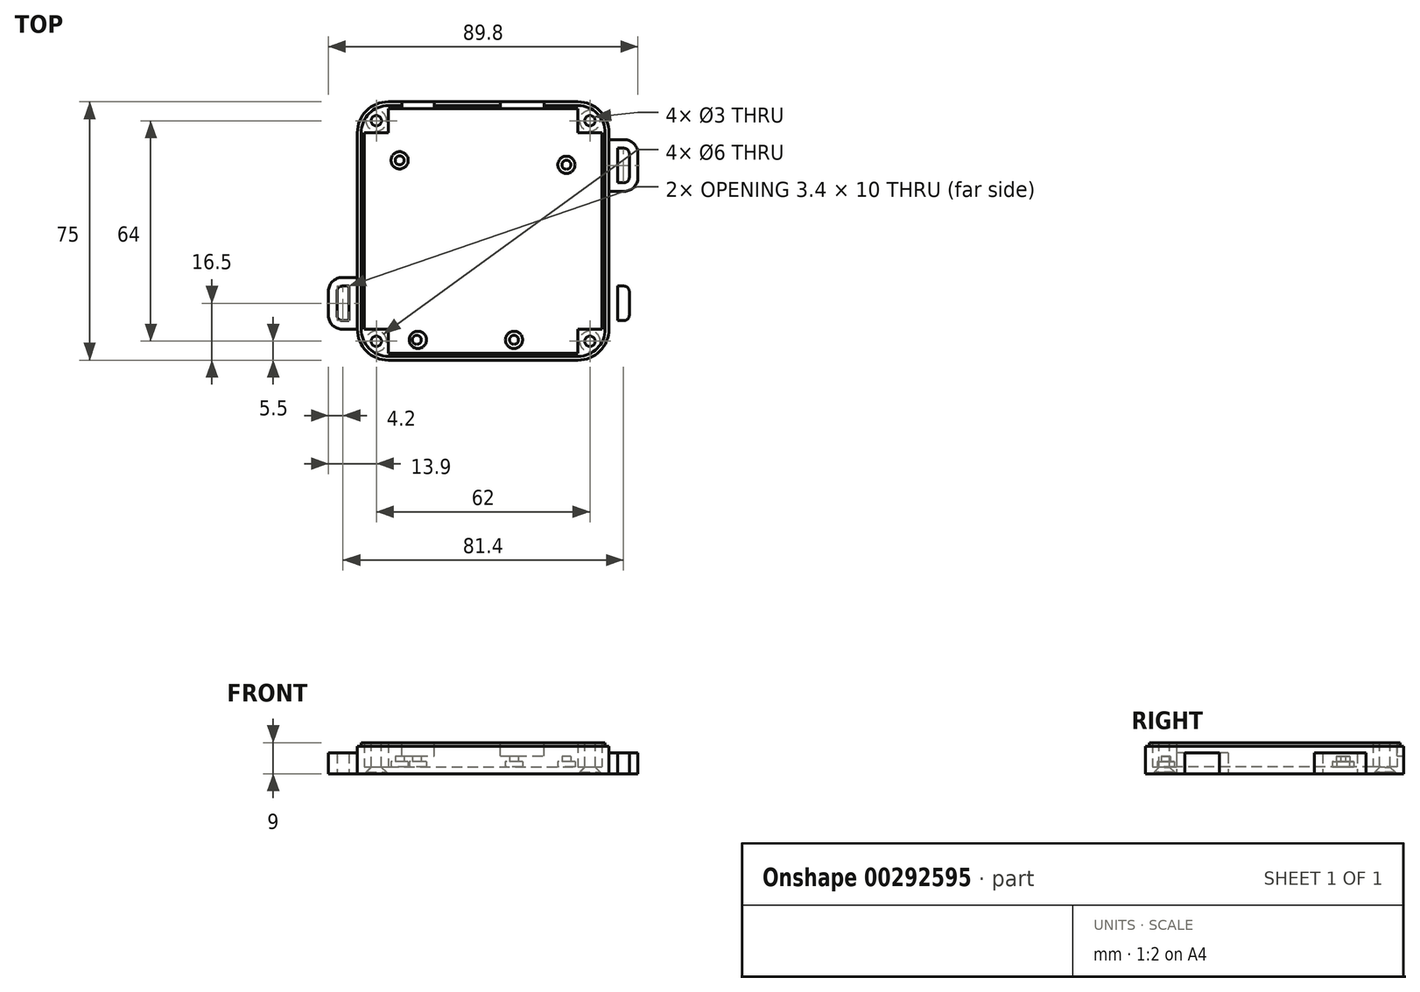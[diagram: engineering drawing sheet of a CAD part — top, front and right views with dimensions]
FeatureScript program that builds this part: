
annotation { "Feature Type Name" : "Feature", "Feature Type Description" : "" }
export const myFeature = defineFeature(function(context is Context, id is Id, definition is map)
    precondition{}
    {
        {
            var Q0;
            Q0=qCreatedBy(makeId("Top.planeOp"),FACE);
            var sketch = newSketch(context, id + "F0", { "sketchPlane" : qUnion([Q0])});
            skLineSegment(sketch, "E0.bottom", {"start": v(-27.5, 38.5) * mm, "end": v(27.5, 38.5) * mm});
            skLineSegment(sketch, "E0.top", {"start": v(-27.5, -36.5) * mm, "end": v(27.5, -36.5) * mm});
            skLineSegment(sketch, "E0.left", {"start": v(-36.5, -12.5) * mm, "end": v(-36.5, -27.5) * mm});
            skLineSegment(sketch, "E0.right", {"start": v(36.5, 29.5) * mm, "end": v(36.5, -27.5) * mm});
            skPoint(sketch, "E1.visualSharp", {"position": v(-36.5, 38.5) * mm});
            skArc(sketch, "E1.filletArc", {"start": v(-27.5, 38.5) * mm, "mid": v(-33.86, 35.86) * mm, "end": v(-36.5, 29.5) * mm});
            skPoint(sketch, "E2.visualSharp", {"position": v(36.5, 38.5) * mm});
            skArc(sketch, "E2.filletArc", {"start": v(36.5, 29.5) * mm, "mid": v(33.86, 35.86) * mm, "end": v(27.5, 38.5) * mm});
            skPoint(sketch, "E3.visualSharp", {"position": v(36.5, -36.5) * mm});
            skArc(sketch, "E3.filletArc", {"start": v(27.5, -36.5) * mm, "mid": v(33.86, -33.86) * mm, "end": v(36.5, -27.5) * mm});
            skPoint(sketch, "E4.visualSharp", {"position": v(-36.5, -36.5) * mm});
            skArc(sketch, "E4.filletArc", {"start": v(-36.5, -27.5) * mm, "mid": v(-33.86, -33.86) * mm, "end": v(-27.5, -36.5) * mm});
            skLineSegment(sketch, "E5.bottom", {"start": v(-36.5, -27.5) * mm, "end": v(-40.9, -27.5) * mm});
            skLineSegment(sketch, "E5.top", {"start": v(-36.5, -12.5) * mm, "end": v(-40.9, -12.5) * mm});
            skLineSegment(sketch, "E5.left", {"start": v(-36.5, -27.5) * mm, "end": v(-36.5, -12.5) * mm});
            skLineSegment(sketch, "E5.right", {"start": v(-44.9, -23.5) * mm, "end": v(-44.9, -16.5) * mm});
            skPoint(sketch, "E6.visualSharp", {"position": v(-44.9, -12.5) * mm});
            skArc(sketch, "E6.filletArc", {"start": v(-40.9, -12.5) * mm, "mid": v(-43.73, -13.67) * mm, "end": v(-44.9, -16.5) * mm});
            skPoint(sketch, "E7.visualSharp", {"position": v(-44.9, -27.5) * mm});
            skArc(sketch, "E7.filletArc", {"start": v(-44.9, -23.5) * mm, "mid": v(-43.73, -26.33) * mm, "end": v(-40.9, -27.5) * mm});
            skLineSegment(sketch, "E8.0", {"start": v(-39, -25) * mm, "end": v(-39, -15) * mm});
            skArc(sketch, "E8.1", {"start": v(-40.9, -15) * mm, "mid": v(-41.96, -15.44) * mm, "end": v(-42.4, -16.5) * mm});
            skLineSegment(sketch, "E8.2", {"start": v(-42.4, -23.5) * mm, "end": v(-42.4, -16.5) * mm});
            skLineSegment(sketch, "E8.3", {"start": v(-39, -15) * mm, "end": v(-40.9, -15) * mm});
            skArc(sketch, "E8.4", {"start": v(-42.4, -23.5) * mm, "mid": v(-41.96, -24.56) * mm, "end": v(-40.9, -25) * mm});
            skLineSegment(sketch, "E8.5", {"start": v(-39, -25) * mm, "end": v(-40.9, -25) * mm});
            skLineSegment(sketch, "E9", {"start": v(-36.5, -27.5) * mm, "end": v(-36.5, 29.5) * mm});
            skArc(sketch, "E10.MirrorCS", {"start": v(-40.9, 12.5) * mm, "mid": v(-43.73, 13.67) * mm, "end": v(-44.9, 16.5) * mm});
            skLineSegment(sketch, "E11.MirrorCS", {"start": v(-36.5, 12.5) * mm, "end": v(-40.9, 12.5) * mm});
            skLineSegment(sketch, "E12.MirrorCS", {"start": v(-39, 25) * mm, "end": v(-39, 15) * mm});
            skLineSegment(sketch, "E13.MirrorCS", {"start": v(-39, 15) * mm, "end": v(-40.9, 15) * mm});
            skArc(sketch, "E14.MirrorCS", {"start": v(-40.9, 15) * mm, "mid": v(-41.96, 15.44) * mm, "end": v(-42.4, 16.5) * mm});
            skLineSegment(sketch, "E15.MirrorCS", {"start": v(-44.9, 23.5) * mm, "end": v(-44.9, 16.5) * mm});
            skArc(sketch, "E16.MirrorCS", {"start": v(-44.9, 23.5) * mm, "mid": v(-43.73, 26.33) * mm, "end": v(-40.9, 27.5) * mm});
            skLineSegment(sketch, "E17.MirrorCS", {"start": v(-36.5, 27.5) * mm, "end": v(-40.9, 27.5) * mm});
            skLineSegment(sketch, "E18.MirrorCS", {"start": v(-39, 25) * mm, "end": v(-40.9, 25) * mm});
            skArc(sketch, "E19.MirrorCS", {"start": v(-42.4, 23.5) * mm, "mid": v(-41.96, 24.56) * mm, "end": v(-40.9, 25) * mm});
            skLineSegment(sketch, "E20.MirrorCS", {"start": v(-42.4, 23.5) * mm, "end": v(-42.4, 16.5) * mm});
            skArc(sketch, "E21.MirrorCS", {"start": v(40.9, -15) * mm, "mid": v(41.96, -15.44) * mm, "end": v(42.4, -16.5) * mm});
            skLineSegment(sketch, "E22.MirrorCS", {"start": v(39, -15) * mm, "end": v(40.9, -15) * mm});
            skArc(sketch, "E23.MirrorCS", {"start": v(42.4, -23.5) * mm, "mid": v(41.96, -24.56) * mm, "end": v(40.9, -25) * mm});
            skLineSegment(sketch, "E24.MirrorCS", {"start": v(39, 15) * mm, "end": v(40.9, 15) * mm});
            skArc(sketch, "E25.MirrorCS", {"start": v(42.4, 23.5) * mm, "mid": v(41.96, 24.56) * mm, "end": v(40.9, 25) * mm});
            skArc(sketch, "E26.MirrorCS", {"start": v(40.9, 15) * mm, "mid": v(41.96, 15.44) * mm, "end": v(42.4, 16.5) * mm});
            skLineSegment(sketch, "E27.MirrorCS", {"start": v(39, -25) * mm, "end": v(40.9, -25) * mm});
            skLineSegment(sketch, "E28.MirrorCS", {"start": v(39, 25) * mm, "end": v(40.9, 25) * mm});
            skArc(sketch, "E29.MirrorCS", {"start": v(40.9, 12.5) * mm, "mid": v(43.73, 13.67) * mm, "end": v(44.9, 16.5) * mm});
            skLineSegment(sketch, "E30.MirrorCS", {"start": v(44.9, 23.5) * mm, "end": v(44.9, 16.5) * mm});
            skLineSegment(sketch, "E31.MirrorCS", {"start": v(42.4, 23.5) * mm, "end": v(42.4, 16.5) * mm});
            skLineSegment(sketch, "E32.MirrorCS", {"start": v(42.4, -23.5) * mm, "end": v(42.4, -16.5) * mm});
            skPoint(sketch, "E33.MirrorP", {"position": v(44.9, -27.5) * mm});
            skLineSegment(sketch, "E34.MirrorCS", {"start": v(44.9, -23.5) * mm, "end": v(44.9, -16.5) * mm});
            skArc(sketch, "E35.MirrorCS", {"start": v(44.9, 23.5) * mm, "mid": v(43.73, 26.33) * mm, "end": v(40.9, 27.5) * mm});
            skLineSegment(sketch, "E36.MirrorCS", {"start": v(39, 25) * mm, "end": v(39, 15) * mm});
            skArc(sketch, "E37.MirrorCS", {"start": v(40.9, -12.5) * mm, "mid": v(43.73, -13.67) * mm, "end": v(44.9, -16.5) * mm});
            skPoint(sketch, "E38.MirrorP", {"position": v(44.9, -12.5) * mm});
            skLineSegment(sketch, "E39.MirrorCS", {"start": v(39, -25) * mm, "end": v(39, -15) * mm});
            skArc(sketch, "E40.MirrorCS", {"start": v(44.9, -23.5) * mm, "mid": v(43.73, -26.33) * mm, "end": v(40.9, -27.5) * mm});
            skLineSegment(sketch, "E41.MirrorCS", {"start": v(36.5, -12.5) * mm, "end": v(36.5, -27.5) * mm});
            skLineSegment(sketch, "E42.MirrorCS", {"start": v(36.5, -27.5) * mm, "end": v(36.5, -12.5) * mm});
            skLineSegment(sketch, "E43.MirrorCS", {"start": v(36.5, -12.5) * mm, "end": v(40.9, -12.5) * mm});
            skLineSegment(sketch, "E44.MirrorCS", {"start": v(36.5, 12.5) * mm, "end": v(40.9, 12.5) * mm});
            skLineSegment(sketch, "E45.MirrorCS", {"start": v(36.5, -27.5) * mm, "end": v(36.5, 29.5) * mm});
            skLineSegment(sketch, "E46.MirrorCS", {"start": v(36.5, -27.5) * mm, "end": v(40.9, -27.5) * mm});
            skLineSegment(sketch, "E47.MirrorCS", {"start": v(36.5, 27.5) * mm, "end": v(40.9, 27.5) * mm});
            skSolve(sketch);
        }
        {
            var Q0;
            Q0=makeQuery(id+"F0.imprint","IMPRINT",FACE,{"disambiguationData":[TD([[makeQuery(id+"F0.imprint","IMPRINT",EDGE,{"derivedFrom":sQuery(id+"F0.wireOp",EDGE,"E0.bottom")}),-1.0]])]});
            extrude(context, id + "F1", {"entities" : qUnion([Q0]), "depth" : 2 * mm});
        }
        {
            var Q0;
            Q0=makeQuery(id+"F0.imprint","IMPRINT",FACE,{"disambiguationData":[TD([[makeQuery(id+"F0.imprint","IMPRINT",EDGE,{"derivedFrom":sQuery(id+"F0.wireOp",EDGE,"E10.MirrorCS")}),-1.0]])]});
            var Q1;
            {var subQ0=sQuery(id+"F0.wireOp",EDGE,"E5.bottom");Q1=makeQuery(id+"F0.imprint","IMPRINT",FACE,{"disambiguationData":[TD([[makeQuery(id+"F0.imprint","IMPRINT",EDGE,{"derivedFrom":subQ0}),-1.0]])]});}
            var Q2;
            Q2=makeQuery(id+"F0.imprint","IMPRINT",FACE,{"disambiguationData":[TD([[makeQuery(id+"F0.imprint","IMPRINT",EDGE,{"derivedFrom":sQuery(id+"F0.wireOp",EDGE,"E25.MirrorCS")}),-1.0]])]});
            var Q3;
            Q3=makeQuery(id+"F0.imprint","IMPRINT",FACE,{"disambiguationData":[TD([[makeQuery(id+"F0.imprint","IMPRINT",EDGE,{"derivedFrom":sQuery(id+"F0.wireOp",EDGE,"E21.MirrorCS")}),1.0]])]});
            extrude(context, id + "F2", {"entities" : qUnion([Q0, Q1, Q2, Q3]), "operationType" : NewBodyOperationType.ADD, "depth" : 6 * mm});
        }
        {
            var Q0;
            Q0=makeQuery(id+"F1.opExtrude","CAP_FACE",FACE,{"disambiguationData":[OSD([sQuery(id+"F0.wireOp",EDGE,"E0.bottom"),sQuery(id+"F0.wireOp",EDGE,"E0.top"),sQuery(id+"F0.wireOp",EDGE,"E0.left"),sQuery(id+"F0.wireOp",EDGE,"E0.right")])],"isStart":false});
            var sketch = newSketch(context, id + "F3", { "sketchPlane" : qUnion([Q0])});
            skCircle(sketch, "E48", {"center": v(-18.94, -30.6) * mm, "radius": 2.5 * mm});
            skCircle(sketch, "E49", {"center": v(8.96, -30.6) * mm, "radius": 2.5 * mm});
            skCircle(sketch, "E50", {"center": v(24.16, 20.2) * mm, "radius": 2.5 * mm});
            skCircle(sketch, "E51", {"center": v(-24.24, 21.5) * mm, "radius": 2.5 * mm});
            skSolve(sketch);
        }
        {
            var Q0;
            Q0=qSketchRegion(id+"F3",true);
            extrude(context, id + "F4", {"entities" : qUnion([Q0]), "operationType" : NewBodyOperationType.ADD, "depth" : 1.5 * mm});
        }
        {
            var Q0;
            Q0=makeQuery(id+"F4.opExtrude","CAP_FACE",FACE,{"disambiguationData":[OSD([sQuery(id+"F3.wireOp",EDGE,"E51")])],"isStart":false});
            var sketch = newSketch(context, id + "F5", { "sketchPlane" : qUnion([Q0])});
            skCircle(sketch, "E52", {"center": v(-19.24, -30.6) * mm, "radius": 1.3 * mm});
            skCircle(sketch, "E53", {"center": v(8.96, -30.6) * mm, "radius": 1.3 * mm});
            skCircle(sketch, "E54", {"center": v(24.16, 20.2) * mm, "radius": 1.3 * mm});
            skCircle(sketch, "E55", {"center": v(-24.24, 21.5) * mm, "radius": 1.3 * mm});
            skSolve(sketch);
        }
        {
            var Q0;
            Q0=qSketchRegion(id+"F5",true);
            extrude(context, id + "F6", {"entities" : qUnion([Q0]), "operationType" : NewBodyOperationType.ADD, "depth" : 1.5 * mm});
        }
        {
            var Q0;
            Q0=makeQuery(id+"F1.opExtrude","CAP_FACE",FACE,{"disambiguationData":[OSD([sQuery(id+"F0.wireOp",EDGE,"E0.bottom"),sQuery(id+"F0.wireOp",EDGE,"E0.top"),sQuery(id+"F0.wireOp",EDGE,"E0.left"),sQuery(id+"F0.wireOp",EDGE,"E0.right"),sQuery(id+"F0.wireOp",EDGE,"E1.filletArc"),sQuery(id+"F0.wireOp",EDGE,"E2.filletArc"),sQuery(id+"F0.wireOp",EDGE,"E3.filletArc"),sQuery(id+"F0.wireOp",EDGE,"E4.filletArc")])],"isStart":false});
            var sketch = newSketch(context, id + "F7", { "sketchPlane" : qUnion([Q0])});
            skLineSegment(sketch, "E56.bottom", {"start": v(-27.5, 38.5) * mm, "end": v(27.5, 38.5) * mm});
            skLineSegment(sketch, "E56.top", {"start": v(-27.5, -36.5) * mm, "end": v(27.5, -36.5) * mm});
            skLineSegment(sketch, "E56.left", {"start": v(-36.5, 29.5) * mm, "end": v(-36.5, -27.5) * mm});
            skLineSegment(sketch, "E56.right", {"start": v(36.5, 29.5) * mm, "end": v(36.5, -27.5) * mm});
            skPoint(sketch, "E57.visualSharp", {"position": v(-36.5, 38.5) * mm});
            skArc(sketch, "E57.filletArc", {"start": v(-27.5, 38.5) * mm, "mid": v(-33.86, 35.86) * mm, "end": v(-36.5, 29.5) * mm});
            skPoint(sketch, "E58.visualSharp", {"position": v(36.5, 38.5) * mm});
            skArc(sketch, "E58.filletArc", {"start": v(36.5, 29.5) * mm, "mid": v(33.86, 35.86) * mm, "end": v(27.5, 38.5) * mm});
            skPoint(sketch, "E59.visualSharp", {"position": v(36.5, -36.5) * mm});
            skArc(sketch, "E59.filletArc", {"start": v(27.5, -36.5) * mm, "mid": v(33.86, -33.86) * mm, "end": v(36.5, -27.5) * mm});
            skPoint(sketch, "E60.visualSharp", {"position": v(-36.5, -36.5) * mm});
            skArc(sketch, "E60.filletArc", {"start": v(-36.5, -27.5) * mm, "mid": v(-33.86, -33.86) * mm, "end": v(-27.5, -36.5) * mm});
            skLineSegment(sketch, "E61", {"start": v(-27.5, 36.5) * mm, "end": v(27.5, 36.5) * mm});
            skLineSegment(sketch, "E62", {"start": v(-34.5, 29.5) * mm, "end": v(-34.5, -27.5) * mm});
            skLineSegment(sketch, "E63", {"start": v(-27.5, -34.5) * mm, "end": v(27.5, -34.5) * mm});
            skLineSegment(sketch, "E64", {"start": v(34.5, 29.5) * mm, "end": v(34.5, -27.5) * mm});
            skLineSegment(sketch, "E65", {"start": v(-34.5, 29.5) * mm, "end": v(-27.5, 29.5) * mm});
            skLineSegment(sketch, "E66", {"start": v(-27.5, 36.5) * mm, "end": v(-27.5, 29.5) * mm});
            skLineSegment(sketch, "E67", {"start": v(27.5, 36.5) * mm, "end": v(27.5, 29.5) * mm});
            skLineSegment(sketch, "E68", {"start": v(27.5, 29.5) * mm, "end": v(34.5, 29.5) * mm});
            skLineSegment(sketch, "E69", {"start": v(-34.5, -27.5) * mm, "end": v(-27.5, -27.5) * mm});
            skLineSegment(sketch, "E70", {"start": v(-27.5, -34.5) * mm, "end": v(-27.5, -27.5) * mm});
            skLineSegment(sketch, "E71", {"start": v(27.5, -34.5) * mm, "end": v(27.5, -27.5) * mm});
            skLineSegment(sketch, "E72", {"start": v(27.5, -27.5) * mm, "end": v(34.5, -27.5) * mm});
            skSolve(sketch);
        }
        {
            var Q0;
            Q0=qSketchRegion(id+"F7",true);
            extrude(context, id + "F8", {"entities" : qUnion([Q0]), "operationType" : NewBodyOperationType.ADD, "depth" : 7 * mm});
        }
        {
            var Q0;
            Q0=makeQuery(id+"F8.opExtrude","CAP_FACE",FACE,{"disambiguationData":[OSD([sQuery(id+"F7.wireOp",EDGE,"E56.bottom"),sQuery(id+"F7.wireOp",EDGE,"E56.top"),sQuery(id+"F7.wireOp",EDGE,"E56.left"),sQuery(id+"F7.wireOp",EDGE,"E56.right"),sQuery(id+"F7.wireOp",EDGE,"E57.filletArc"),sQuery(id+"F7.wireOp",EDGE,"E58.filletArc"),sQuery(id+"F7.wireOp",EDGE,"E59.filletArc"),sQuery(id+"F7.wireOp",EDGE,"E60.filletArc"),sQuery(id+"F7.wireOp",EDGE,"E61"),sQuery(id+"F7.wireOp",EDGE,"E62"),sQuery(id+"F7.wireOp",EDGE,"E63"),sQuery(id+"F7.wireOp",EDGE,"E64"),sQuery(id+"F7.wireOp",EDGE,"E65"),sQuery(id+"F7.wireOp",EDGE,"E66"),sQuery(id+"F7.wireOp",EDGE,"E67"),sQuery(id+"F7.wireOp",EDGE,"E68"),sQuery(id+"F7.wireOp",EDGE,"E69"),sQuery(id+"F7.wireOp",EDGE,"E70"),sQuery(id+"F7.wireOp",EDGE,"E71"),sQuery(id+"F7.wireOp",EDGE,"E72")])],"isStart":false});
            var sketch = newSketch(context, id + "F9", { "sketchPlane" : qUnion([Q0])});
            skCircle(sketch, "E73", {"center": v(-31, 33) * mm, "radius": 1.5 * mm});
            skCircle(sketch, "E74", {"center": v(31, 33) * mm, "radius": 1.5 * mm});
            skCircle(sketch, "E75", {"center": v(-31, -31) * mm, "radius": 1.5 * mm});
            skCircle(sketch, "E76", {"center": v(31, -31) * mm, "radius": 1.5 * mm});
            skSolve(sketch);
        }
        {
            var Q0;
            Q0=qSketchRegion(id+"F9",true);
            extrude(context, id + "F10", {"entities" : qUnion([Q0]), "operationType" : NewBodyOperationType.REMOVE, "oppositeDirection" : true, "depth" : 10 * mm});
        }
        {
            var Q0;
            Q0=makeQuery(id+"F8.opExtrude","CAP_FACE",FACE,{"disambiguationData":[OSD([sQuery(id+"F7.wireOp",EDGE,"E56.bottom"),sQuery(id+"F7.wireOp",EDGE,"E56.top"),sQuery(id+"F7.wireOp",EDGE,"E56.left"),sQuery(id+"F7.wireOp",EDGE,"E56.right"),sQuery(id+"F7.wireOp",EDGE,"E57.filletArc"),sQuery(id+"F7.wireOp",EDGE,"E58.filletArc"),sQuery(id+"F7.wireOp",EDGE,"E59.filletArc"),sQuery(id+"F7.wireOp",EDGE,"E60.filletArc"),sQuery(id+"F7.wireOp",EDGE,"E61"),sQuery(id+"F7.wireOp",EDGE,"E62"),sQuery(id+"F7.wireOp",EDGE,"E63"),sQuery(id+"F7.wireOp",EDGE,"E64"),sQuery(id+"F7.wireOp",EDGE,"E65"),sQuery(id+"F7.wireOp",EDGE,"E66"),sQuery(id+"F7.wireOp",EDGE,"E67"),sQuery(id+"F7.wireOp",EDGE,"E68"),sQuery(id+"F7.wireOp",EDGE,"E69"),sQuery(id+"F7.wireOp",EDGE,"E70"),sQuery(id+"F7.wireOp",EDGE,"E71"),sQuery(id+"F7.wireOp",EDGE,"E72")])],"isStart":false});
            var sketch = newSketch(context, id + "F11", { "sketchPlane" : qUnion([Q0])});
            skLineSegment(sketch, "E77.bottom", {"start": v(17.66, 36.5) * mm, "end": v(5.06, 36.5) * mm});
            skLineSegment(sketch, "E77.top", {"start": v(17.66, 38.5) * mm, "end": v(5.06, 38.5) * mm});
            skLineSegment(sketch, "E77.left", {"start": v(17.66, 36.5) * mm, "end": v(17.66, 38.5) * mm});
            skLineSegment(sketch, "E77.right", {"start": v(5.06, 36.5) * mm, "end": v(5.06, 38.5) * mm});
            skLineSegment(sketch, "E78.bottom", {"start": v(-14.14, 36.5) * mm, "end": v(-23.64, 36.5) * mm});
            skLineSegment(sketch, "E78.top", {"start": v(-14.14, 38.5) * mm, "end": v(-23.64, 38.5) * mm});
            skLineSegment(sketch, "E78.left", {"start": v(-14.14, 36.5) * mm, "end": v(-14.14, 38.5) * mm});
            skLineSegment(sketch, "E78.right", {"start": v(-23.64, 36.5) * mm, "end": v(-23.64, 38.5) * mm});
            skSolve(sketch);
        }
        {
            var Q0;
            Q0=qSketchRegion(id+"F11",true);
            extrude(context, id + "F12", {"entities" : qUnion([Q0]), "operationType" : NewBodyOperationType.REMOVE, "oppositeDirection" : true, "depth" : 3.8 * mm});
        }
        {
            var Q0;
            Q0=makeQuery(id+"F1.opExtrude","CAP_FACE",FACE,{"disambiguationData":[OSD([sQuery(id+"F0.wireOp",EDGE,"E0.bottom"),sQuery(id+"F0.wireOp",EDGE,"E0.top"),sQuery(id+"F0.wireOp",EDGE,"E0.left"),sQuery(id+"F0.wireOp",EDGE,"E0.right"),sQuery(id+"F0.wireOp",EDGE,"E1.filletArc"),sQuery(id+"F0.wireOp",EDGE,"E2.filletArc"),sQuery(id+"F0.wireOp",EDGE,"E3.filletArc"),sQuery(id+"F0.wireOp",EDGE,"E4.filletArc")])],"isStart":true});
            var sketch = newSketch(context, id + "F13", { "sketchPlane" : qUnion([Q0])});
            skCircle(sketch, "E79", {"center": v(31, -33) * mm, "radius": 3 * mm});
            skCircle(sketch, "E80", {"center": v(-31, -33) * mm, "radius": 3 * mm});
            skCircle(sketch, "E81", {"center": v(-31, 31) * mm, "radius": 3 * mm});
            skCircle(sketch, "E82", {"center": v(31, 31) * mm, "radius": 3 * mm});
            skSolve(sketch);
        }
        {
            var Q0;
            Q0=qSketchRegion(id+"F13",true);
            extrude(context, id + "F14", {"entities" : qUnion([Q0]), "operationType" : NewBodyOperationType.REMOVE, "oppositeDirection" : true, "depth" : .4 * mm});
        }
        {
            var Q0;
            Q0=makeQuery(id+"F14.boolean.opBoolean","INTERSECT",EDGE,{"derivedFrom":[makeQuery(id+"F10.boolean.opBoolean","COPY",FACE,{"derivedFrom":makeQuery(id+"F10.opExtrude","SWEPT_FACE",FACE,{"disambiguationData":[OSD([sQuery(id+"F9.wireOp",EDGE,"E74")])]})}),makeQuery(id+"F14.opExtrude","CAP_FACE",FACE,{"disambiguationData":[OSD([sQuery(id+"F13.wireOp",EDGE,"E79")])],"isStart":false})]});
            var Q1;
            Q1=makeQuery(id+"F14.boolean.opBoolean","INTERSECT",EDGE,{"derivedFrom":[makeQuery(id+"F10.boolean.opBoolean","COPY",FACE,{"derivedFrom":makeQuery(id+"F10.opExtrude","SWEPT_FACE",FACE,{"disambiguationData":[OSD([sQuery(id+"F9.wireOp",EDGE,"E73")])]})}),makeQuery(id+"F14.opExtrude","CAP_FACE",FACE,{"disambiguationData":[OSD([sQuery(id+"F13.wireOp",EDGE,"E80")])],"isStart":false})]});
            var Q2;
            Q2=makeQuery(id+"F14.boolean.opBoolean","INTERSECT",EDGE,{"derivedFrom":[makeQuery(id+"F10.boolean.opBoolean","COPY",FACE,{"derivedFrom":makeQuery(id+"F10.opExtrude","SWEPT_FACE",FACE,{"disambiguationData":[OSD([sQuery(id+"F9.wireOp",EDGE,"E76")])]})}),makeQuery(id+"F14.opExtrude","CAP_FACE",FACE,{"disambiguationData":[OSD([sQuery(id+"F13.wireOp",EDGE,"E82")])],"isStart":false})]});
            var Q3;
            Q3=makeQuery(id+"F14.boolean.opBoolean","INTERSECT",EDGE,{"derivedFrom":[makeQuery(id+"F10.boolean.opBoolean","COPY",FACE,{"derivedFrom":makeQuery(id+"F10.opExtrude","SWEPT_FACE",FACE,{"disambiguationData":[OSD([sQuery(id+"F9.wireOp",EDGE,"E75")])]})}),makeQuery(id+"F14.opExtrude","CAP_FACE",FACE,{"disambiguationData":[OSD([sQuery(id+"F13.wireOp",EDGE,"E81")])],"isStart":false})]});
            chamfer(context, id + "F15", {"entities" : qUnion([Q0, Q1, Q2, Q3]), "width" : 1.5 * mm, "tangentPropagation" : true});
        }
        {
            var Q0;
            {var subQ0=sQuery(id+"F7.wireOp",EDGE,"E56.bottom");var subQ1=sQuery(id+"F7.wireOp",EDGE,"E56.top");var subQ2=sQuery(id+"F7.wireOp",EDGE,"E56.left");var subQ3=sQuery(id+"F7.wireOp",EDGE,"E56.right");var subQ4=sQuery(id+"F7.wireOp",EDGE,"E57.filletArc");var subQ5=sQuery(id+"F7.wireOp",EDGE,"E58.filletArc");var subQ6=sQuery(id+"F7.wireOp",EDGE,"E59.filletArc");var subQ7=sQuery(id+"F7.wireOp",EDGE,"E60.filletArc");var subQ8=sQuery(id+"F7.wireOp",EDGE,"E61");var subQ9=sQuery(id+"F7.wireOp",EDGE,"E62");var subQ10=sQuery(id+"F7.wireOp",EDGE,"E63");var subQ11=sQuery(id+"F7.wireOp",EDGE,"E64");var subQ12=sQuery(id+"F7.wireOp",EDGE,"E65");var subQ13=sQuery(id+"F7.wireOp",EDGE,"E66");var subQ14=sQuery(id+"F7.wireOp",EDGE,"E67");var subQ15=sQuery(id+"F7.wireOp",EDGE,"E68");var subQ16=sQuery(id+"F7.wireOp",EDGE,"E69");var subQ17=sQuery(id+"F7.wireOp",EDGE,"E70");var subQ18=sQuery(id+"F7.wireOp",EDGE,"E71");var subQ19=sQuery(id+"F7.wireOp",EDGE,"E72");Q0=makeQuery(id+"F12.boolean.opBoolean","SPLIT",FACE,{"disambiguationData":[TD([makeQuery(id+"F1.opExtrude","SWEPT_FACE",FACE,{"disambiguationData":[OSD([sQuery(id+"F0.wireOp",EDGE,"E0.top")])]})])],"derivedFrom":makeQuery(id+"F8.opExtrude","CAP_FACE",FACE,{"disambiguationData":[OSD([subQ0,subQ1,subQ2,subQ3,subQ4,subQ5,subQ6,subQ7,subQ8,subQ9,subQ10,subQ11,subQ12,subQ13,subQ14,subQ15,subQ16,subQ17,subQ18,subQ19])],"isStart":false})});}
            var sketch = newSketch(context, id + "F16", { "sketchPlane" : qUnion([Q0])});
            skLineSegment(sketch, "E83.0", {"start": v(-27.5, 38.5) * mm, "end": v(-23.64, 38.5) * mm});
            skArc(sketch, "E83.1", {"start": v(-27.5, 38.5) * mm, "mid": v(-33.86, 35.86) * mm, "end": v(-36.5, 29.5) * mm});
            skLineSegment(sketch, "E83.2", {"start": v(-36.5, 29.5) * mm, "end": v(-36.5, -27.5) * mm});
            skArc(sketch, "E83.3", {"start": v(-36.5, -27.5) * mm, "mid": v(-33.86, -33.86) * mm, "end": v(-27.5, -36.5) * mm});
            skLineSegment(sketch, "E83.4", {"start": v(-27.5, -36.5) * mm, "end": v(27.5, -36.5) * mm});
            skArc(sketch, "E83.5", {"start": v(27.5, -36.5) * mm, "mid": v(33.86, -33.86) * mm, "end": v(36.5, -27.5) * mm});
            skLineSegment(sketch, "E83.6", {"start": v(36.5, 29.5) * mm, "end": v(36.5, -27.5) * mm});
            skArc(sketch, "E83.7", {"start": v(36.5, 29.5) * mm, "mid": v(33.86, 35.86) * mm, "end": v(27.5, 38.5) * mm});
            skLineSegment(sketch, "E83.8", {"start": v(17.66, 38.5) * mm, "end": v(27.5, 38.5) * mm});
            skLineSegment(sketch, "E83.9", {"start": v(-14.14, 38.5) * mm, "end": v(5.06, 38.5) * mm});
            skLineSegment(sketch, "E84.top", {"start": v(-14.14, 37.4) * mm, "end": v(5.06, 37.4) * mm});
            skLineSegment(sketch, "E84.left", {"start": v(-14.14, 38.5) * mm, "end": v(-14.14, 37.4) * mm});
            skLineSegment(sketch, "E84.right", {"start": v(5.06, 38.5) * mm, "end": v(5.06, 37.4) * mm});
            skLineSegment(sketch, "E85", {"start": v(-35.4, 29.5) * mm, "end": v(-35.4, -27.5) * mm});
            skLineSegment(sketch, "E86", {"start": v(35.4, 29.5) * mm, "end": v(35.4, -27.5) * mm});
            skLineSegment(sketch, "E87", {"start": v(-27.5, -35.4) * mm, "end": v(27.5, -35.4) * mm});
            skLineSegment(sketch, "E88", {"start": v(-27.5, 37.4) * mm, "end": v(-23.64, 37.4) * mm});
            skLineSegment(sketch, "E89", {"start": v(-23.64, 37.4) * mm, "end": v(-23.64, 38.5) * mm});
            skArc(sketch, "E90", {"start": v(-27.5, 37.4) * mm, "mid": v(-33.09, 35.09) * mm, "end": v(-35.4, 29.5) * mm});
            skLineSegment(sketch, "E91", {"start": v(27.5, 37.4) * mm, "end": v(17.66, 37.4) * mm});
            skLineSegment(sketch, "E92", {"start": v(17.66, 38.5) * mm, "end": v(17.66, 37.4) * mm});
            skArc(sketch, "E93", {"start": v(35.4, 29.5) * mm, "mid": v(33.09, 35.09) * mm, "end": v(27.5, 37.4) * mm});
            skArc(sketch, "E94", {"start": v(27.5, -35.4) * mm, "mid": v(33.09, -33.09) * mm, "end": v(35.4, -27.5) * mm});
            skArc(sketch, "E95", {"start": v(-35.4, -27.5) * mm, "mid": v(-33.09, -33.09) * mm, "end": v(-27.5, -35.4) * mm});
            skSolve(sketch);
        }
        {
            var Q0;
            Q0=qSketchRegion(id+"F16",true);
            extrude(context, id + "F17", {"entities" : qUnion([Q0]), "operationType" : NewBodyOperationType.REMOVE, "oppositeDirection" : true, "depth" : 1 * mm});
        }
    });
